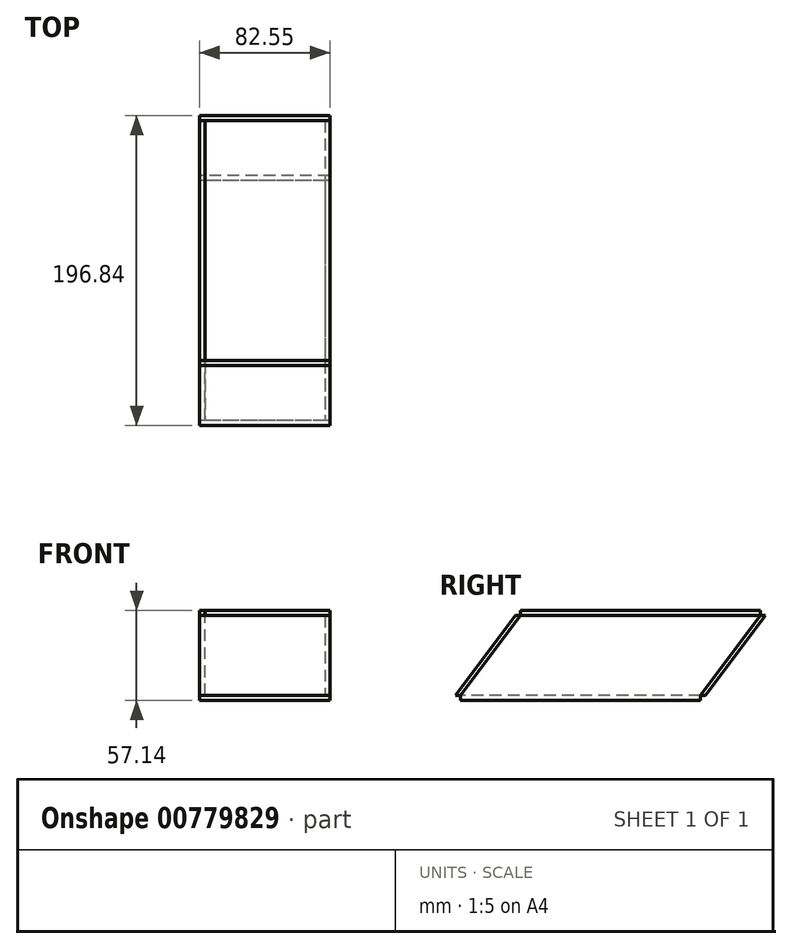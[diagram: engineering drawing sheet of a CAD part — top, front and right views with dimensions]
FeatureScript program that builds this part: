
annotation { "Feature Type Name" : "Feature", "Feature Type Description" : "" }
export const myFeature = defineFeature(function(context is Context, id is Id, definition is map)
    precondition{}
    {
        {
            var Q0;
            Q0=qCreatedBy(makeId("Right.planeOp"),FACE);
            var sketch = newSketch(context, id + "F0", { "sketchPlane" : qUnion([Q0])});
            skLineSegment(sketch, "E0.bottom", {"start": v(95.25, 25.4) * mm, "end": v(-57.15, 25.4) * mm});
            skLineSegment(sketch, "E0.top", {"start": v(57.15, -25.4) * mm, "end": v(-95.25, -25.4) * mm});
            skPoint(sketch, "E0.middle", {"position": v(0, 0) * mm});
            skPoint(sketch, "E1", {"position": v(57.15, -25.4) * mm});
            skLineSegment(sketch, "E2", {"start": v(95.25, 25.4) * mm, "end": v(57.15, -25.4) * mm});
            skPoint(sketch, "E3", {"position": v(-57.15, 25.4) * mm});
            skLineSegment(sketch, "E4", {"start": v(-57.15, 25.4) * mm, "end": v(-95.25, -25.4) * mm});
            skPoint(sketch, "E0.left.end.orphan", {"position": v(95.25, -25.4) * mm});
            skPoint(sketch, "E0.right.start.orphan", {"position": v(-95.25, 25.4) * mm});
            skSolve(sketch);
        }
        {
            var Q0;
            Q0=makeQuery(id+"F0.imprint","IMPRINT",FACE,{"disambiguationData":[TD([[makeQuery(id+"F0.imprint","IMPRINT",EDGE,{"derivedFrom":sQuery(id+"F0.wireOp",EDGE,"E0.bottom")}),1.0]])]});
            extrude(context, id + "F1", {"entities" : qUnion([Q0]), "depth" : 3.17 * mm, "offsetDistance" : 25.4 * mm});
        }
        {
            var Q0;
            Q0=makeQuery(id+"F1.opExtrude","SWEPT_FACE",FACE,{"disambiguationData":[OSD([sQuery(id+"F0.wireOp",EDGE,"E0.bottom")])]});
            var sketch = newSketch(context, id + "F2", { "sketchPlane" : qUnion([Q0])});
            skLineSegment(sketch, "E5.bottom", {"start": v(3.17, -57.15) * mm, "end": v(-79.38, -57.15) * mm});
            skLineSegment(sketch, "E5.top", {"start": v(3.17, 95.25) * mm, "end": v(-79.38, 95.25) * mm});
            skLineSegment(sketch, "E5.left", {"start": v(3.18, -57.15) * mm, "end": v(3.18, 95.25) * mm});
            skLineSegment(sketch, "E5.right", {"start": v(-79.38, -57.15) * mm, "end": v(-79.38, 95.25) * mm});
            skSolve(sketch);
        }
        {
            var Q0;
            {var subQ2=sQuery(id+"F2.wireOp",EDGE,"E5.left");Q0=makeQuery(id+"F2.imprint","IMPRINT",FACE,{"disambiguationData":[TD([[makeQuery(id+"F2.imprint","IMPRINT",EDGE,{"derivedFrom":subQ2}),-1.0]])]});}
            var Q1;
            {var subQ2=sQuery(id+"F2.wireOp",EDGE,"E5.right");Q1=makeQuery(id+"F2.imprint","IMPRINT",FACE,{"disambiguationData":[TD([[makeQuery(id+"F2.imprint","IMPRINT",EDGE,{"derivedFrom":subQ2}),-1.0]])]});}
            extrude(context, id + "F3", {"entities" : qUnion([Q0, Q1]), "depth" : 3.17 * mm, "offsetDistance" : 25.4 * mm});
        }
        {
            var Q0;
            Q0=makeQuery(id+"F1.opExtrude","SWEPT_FACE",FACE,{"disambiguationData":[OSD([sQuery(id+"F0.wireOp",EDGE,"E0.top")])]});
            var sketch = newSketch(context, id + "F4", { "sketchPlane" : qUnion([Q0])});
            skLineSegment(sketch, "E6.bottom", {"start": v(3.17, -57.15) * mm, "end": v(-79.38, -57.15) * mm});
            skLineSegment(sketch, "E6.top", {"start": v(3.17, 95.25) * mm, "end": v(-79.38, 95.25) * mm});
            skLineSegment(sketch, "E6.left", {"start": v(3.18, -57.15) * mm, "end": v(3.18, 95.25) * mm});
            skLineSegment(sketch, "E6.right", {"start": v(-79.38, -57.15) * mm, "end": v(-79.38, 95.25) * mm});
            skSolve(sketch);
        }
        {
            var Q0;
            Q0 = qSketchRegion(id + "F4", true);
            extrude(context, id + "F5", {"entities" : qUnion([Q0]), "operationType" : NewBodyOperationType.ADD, "depth" : 3.17 * mm, "offsetDistance" : 25.4 * mm});
        }
        {
            var Q0;
            Q0=makeQuery(id+"F3.opExtrude","SWEPT_FACE",FACE,{"disambiguationData":[OSD([sQuery(id+"F2.wireOp",EDGE,"E5.right")])]});
            var sketch = newSketch(context, id + "F6", { "sketchPlane" : qUnion([Q0])});
            skLineSegment(sketch, "E7.bottom", {"start": v(-95.25, 25.4) * mm, "end": v(57.15, 25.4) * mm});
            skLineSegment(sketch, "E7.top", {"start": v(-57.15, -25.4) * mm, "end": v(95.25, -25.4) * mm});
            skLineSegment(sketch, "E8", {"start": v(-95.25, 25.4) * mm, "end": v(-57.15, -25.4) * mm});
            skLineSegment(sketch, "E9", {"start": v(95.25, -25.4) * mm, "end": v(57.15, 25.4) * mm});
            skSolve(sketch);
        }
        {
            var Q0;
            Q0 = qSketchRegion(id + "F6", true);
            var Q1;
            Q1=makeQuery(id+"F6.imprint","IMPRINT",FACE,{"disambiguationData":[TD([[makeQuery(id+"F6.imprint","IMPRINT",EDGE,{"derivedFrom":sQuery(id+"F6.wireOp",EDGE,"E7.bottom")}),-1.0]])]});
            extrude(context, id + "F7", {"entities" : qUnion([Q0, Q1]), "oppositeDirection" : true, "depth" : 3.17 * mm, "offsetDistance" : 25.4 * mm});
        }
        {
            var Q0;
            Q0=makeQuery(id+"F7.opExtrude","CAP_FACE",FACE,{"disambiguationData":[OSD([sQuery(id+"F2.wireOp",EDGE,"E5.bottom"),sQuery(id+"F2.wireOp",EDGE,"E5.top"),sQuery(id+"F2.wireOp",EDGE,"E5.right"),sQuery(id+"F6.wireOp",EDGE,"E7.top"),sQuery(id+"F6.wireOp",EDGE,"E8"),sQuery(id+"F6.wireOp",EDGE,"E9")])],"isStart":true});
            var sketch = newSketch(context, id + "F8", { "sketchPlane" : qUnion([Q0])});
            skLineSegment(sketch, "E10", {"start": v(-60.33, -25.4) * mm, "end": v(-57.15, -25.4) * mm});
            skLineSegment(sketch, "E11", {"start": v(-57.15, -25.4) * mm, "end": v(-95.25, 25.4) * mm});
            skLineSegment(sketch, "E12", {"start": v(-95.25, 25.4) * mm, "end": v(-98.43, 25.4) * mm});
            skLineSegment(sketch, "E13", {"start": v(-57.15, -25.4) * mm, "end": v(-60.33, -25.4) * mm});
            skLineSegment(sketch, "E14", {"start": v(-98.43, 25.4) * mm, "end": v(-60.33, -25.4) * mm});
            skSolve(sketch);
        }
        {
            var Q0;
            Q0=makeQuery(id+"F8.imprint","IMPRINT",FACE,{"disambiguationData":[TD([[makeQuery(id+"F8.imprint","IMPRINT",EDGE,{"derivedFrom":sQuery(id+"F8.wireOp",EDGE,"E11")}),-1.0]])]});
            extrude(context, id + "F9", {"entities" : qUnion([Q0]), "oppositeDirection" : true, "depth" : 82.55 * mm, "offsetDistance" : 25.4 * mm});
        }
        {
            var Q0;
            Q0=makeQuery(id+"F7.opExtrude","CAP_FACE",FACE,{"disambiguationData":[OSD([sQuery(id+"F2.wireOp",EDGE,"E5.bottom"),sQuery(id+"F2.wireOp",EDGE,"E5.top"),sQuery(id+"F2.wireOp",EDGE,"E5.right"),sQuery(id+"F6.wireOp",EDGE,"E7.top"),sQuery(id+"F6.wireOp",EDGE,"E8"),sQuery(id+"F6.wireOp",EDGE,"E9")])],"isStart":true});
            var sketch = newSketch(context, id + "F10", { "sketchPlane" : qUnion([Q0])});
            skLineSegment(sketch, "E15", {"start": v(57.15, 25.4) * mm, "end": v(60.33, 25.4) * mm});
            skLineSegment(sketch, "E16", {"start": v(95.25, -25.4) * mm, "end": v(98.42, -25.4) * mm});
            skLineSegment(sketch, "E17", {"start": v(60.33, 25.4) * mm, "end": v(98.42, -25.4) * mm});
            skSolve(sketch);
        }
        {
            var Q0;
            Q0=makeQuery(id+"F10.imprint","IMPRINT",FACE,{"disambiguationData":[TD([[makeQuery(id+"F10.imprint","IMPRINT",EDGE,{"derivedFrom":sQuery(id+"F10.wireOp",EDGE,"E15")}),-1.0]])]});
            extrude(context, id + "F11", {"entities" : qUnion([Q0]), "oppositeDirection" : true, "depth" : 82.55 * mm, "offsetDistance" : 25.4 * mm});
        }
    });
